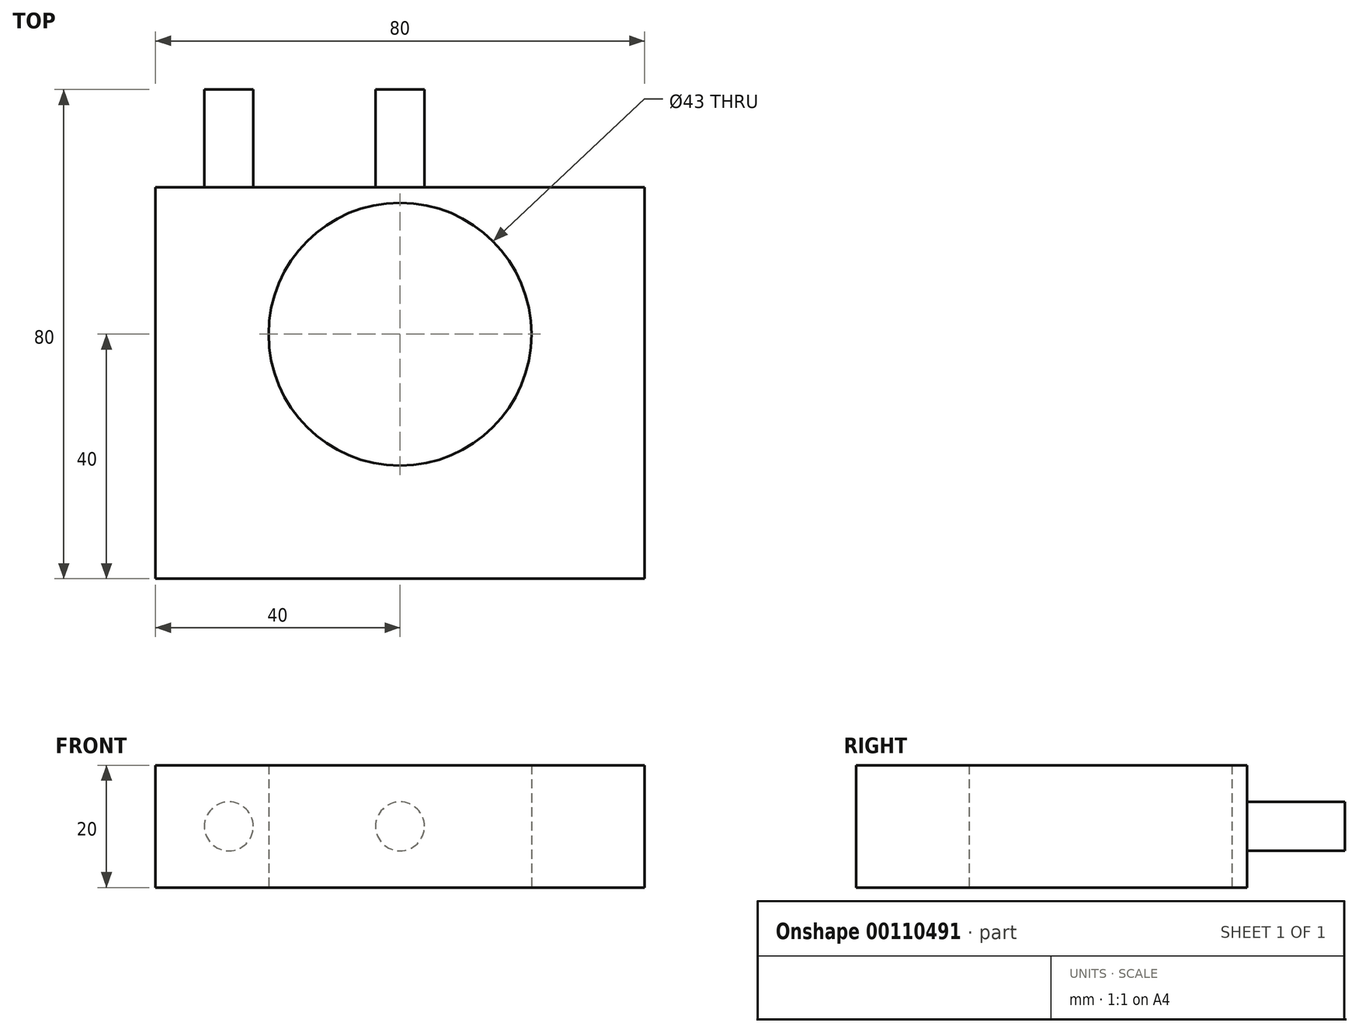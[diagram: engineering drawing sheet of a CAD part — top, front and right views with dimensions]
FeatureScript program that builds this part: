
annotation { "Feature Type Name" : "Feature", "Feature Type Description" : "" }
export const myFeature = defineFeature(function(context is Context, id is Id, definition is map)
    precondition{}
    {
        {
            var Q0;
            Q0=qCreatedBy(makeId("Top.planeOp"),FACE);
            var sketch = newSketch(context, id + "F0", { "sketchPlane" : qUnion([Q0])});
            skLineSegment(sketch, "E0.bottom", {"start": v(0, 0) * mm, "end": v(80, 0) * mm});
            skLineSegment(sketch, "E0.top", {"start": v(0, -80) * mm, "end": v(80, -80) * mm});
            skLineSegment(sketch, "E0.left", {"start": v(0, 0) * mm, "end": v(0, -80) * mm});
            skLineSegment(sketch, "E0.right", {"start": v(80, 0) * mm, "end": v(80, -80) * mm});
            skLineSegment(sketch, "E1", {"start": v(0, -40) * mm, "end": v(80, -40) * mm, "construction": true});
            skCircle(sketch, "E2", {"center": v(40, -40) * mm, "radius": 21.5 * mm});
            skSolve(sketch);
        }
        {
            var Q0;
            Q0=makeQuery(id+"F0.imprint","IMPRINT",FACE,{"disambiguationData":[TD([[makeQuery(id+"F0.imprint","IMPRINT",EDGE,{"derivedFrom":sQuery(id+"F0.wireOp",EDGE,"E0.bottom")}),-1.0]])]});
            extrude(context, id + "F1", {"entities" : qUnion([Q0]), "depth" : 20 * mm});
        }
        {
            var Q0;
            Q0=makeQuery(id+"F1.opExtrude","SWEPT_FACE",FACE,{"disambiguationData":[OSD([sQuery(id+"F0.wireOp",EDGE,"E0.bottom")])]});
            var sketch = newSketch(context, id + "F2", { "sketchPlane" : qUnion([Q0])});
            skLineSegment(sketch, "E3", {"start": v(0, 10) * mm, "end": v(-80, 10) * mm});
            skCircle(sketch, "E4", {"center": v(-40, 10) * mm, "radius": 4 * mm});
            skCircle(sketch, "E5", {"center": v(-68, 10) * mm, "radius": 4 * mm});
            skCircle(sketch, "E6", {"center": v(-12, 10) * mm, "radius": 4 * mm});
            skSolve(sketch);
        }
        {
            var Q0;
            {var subQ0=sQuery(id+"F2.wireOp",EDGE,"E5");var subQ1=sQuery(id+"F2.wireOp",EDGE,"E3");var subQ2=makeQuery(id+"F2.imprint","INTERSECT",VERTEX,{"disambiguationData":[OD(0.0)],"derivedFrom":[subQ1,subQ0]});Q0=makeQuery(id+"F2.imprint","IMPRINT",FACE,{"disambiguationData":[TD([[makeQuery(id+"F2.imprint","IMPRINT",EDGE,{"disambiguationData":[TD([[subQ2,-1.0]])],"derivedFrom":subQ1}),-1.0]])]});}
            var Q1;
            {var subQ0=sQuery(id+"F2.wireOp",EDGE,"E5");var subQ1=sQuery(id+"F2.wireOp",EDGE,"E3");var subQ2=makeQuery(id+"F2.imprint","INTERSECT",VERTEX,{"disambiguationData":[OD(0.0)],"derivedFrom":[subQ1,subQ0]});Q1=makeQuery(id+"F2.imprint","IMPRINT",FACE,{"disambiguationData":[TD([[makeQuery(id+"F2.imprint","IMPRINT",EDGE,{"disambiguationData":[TD([[subQ2,-1.0]])],"derivedFrom":subQ1}),1.0]])]});}
            var Q2;
            {var subQ0=sQuery(id+"F2.wireOp",EDGE,"E6");var subQ1=sQuery(id+"F2.wireOp",EDGE,"E3");var subQ2=makeQuery(id+"F2.imprint","INTERSECT",VERTEX,{"disambiguationData":[OD(0.0)],"derivedFrom":[subQ1,subQ0]});Q2=makeQuery(id+"F2.imprint","IMPRINT",FACE,{"disambiguationData":[TD([[makeQuery(id+"F2.imprint","IMPRINT",EDGE,{"disambiguationData":[TD([[subQ2,-1.0]])],"derivedFrom":subQ1}),1.0]])]});}
            var Q3;
            {var subQ0=sQuery(id+"F2.wireOp",EDGE,"E6");var subQ1=sQuery(id+"F2.wireOp",EDGE,"E3");var subQ2=makeQuery(id+"F2.imprint","INTERSECT",VERTEX,{"disambiguationData":[OD(0.0)],"derivedFrom":[subQ1,subQ0]});Q3=makeQuery(id+"F2.imprint","IMPRINT",FACE,{"disambiguationData":[TD([[makeQuery(id+"F2.imprint","IMPRINT",EDGE,{"disambiguationData":[TD([[subQ2,-1.0]])],"derivedFrom":subQ1}),-1.0]])]});}
            var Q4;
            {var subQ0=sQuery(id+"F2.wireOp",EDGE,"E4");var subQ1=sQuery(id+"F2.wireOp",EDGE,"E3");var subQ2=makeQuery(id+"F2.imprint","INTERSECT",VERTEX,{"disambiguationData":[OD(0.0)],"derivedFrom":[subQ1,subQ0]});Q4=makeQuery(id+"F2.imprint","IMPRINT",FACE,{"disambiguationData":[TD([[makeQuery(id+"F2.imprint","IMPRINT",EDGE,{"disambiguationData":[TD([[subQ2,-1.0]])],"derivedFrom":subQ1}),-1.0]])]});}
            var Q5;
            {var subQ0=sQuery(id+"F2.wireOp",EDGE,"E4");var subQ1=sQuery(id+"F2.wireOp",EDGE,"E3");var subQ2=makeQuery(id+"F2.imprint","INTERSECT",VERTEX,{"disambiguationData":[OD(0.0)],"derivedFrom":[subQ1,subQ0]});Q5=makeQuery(id+"F2.imprint","IMPRINT",FACE,{"disambiguationData":[TD([[makeQuery(id+"F2.imprint","IMPRINT",EDGE,{"disambiguationData":[TD([[subQ2,-1.0]])],"derivedFrom":subQ1}),1.0]])]});}
            extrude(context, id + "F3", {"entities" : qUnion([Q0, Q1, Q2, Q3, Q4, Q5]), "operationType" : NewBodyOperationType.REMOVE, "oppositeDirection" : true, "depth" : 16 * mm});
        }
    });
